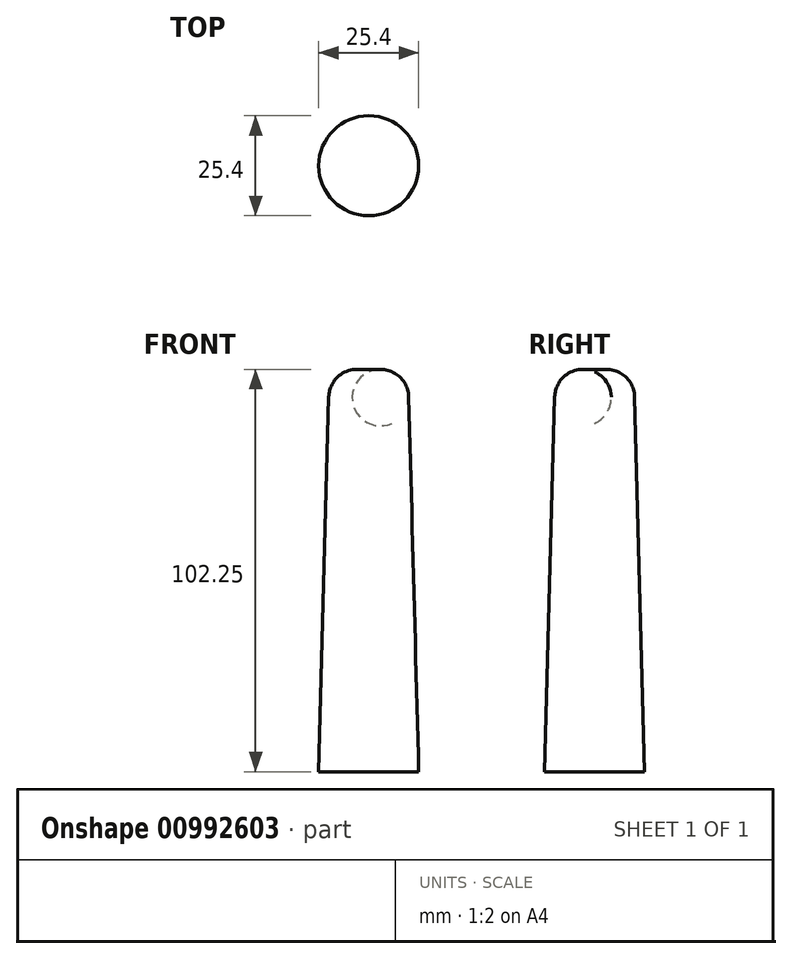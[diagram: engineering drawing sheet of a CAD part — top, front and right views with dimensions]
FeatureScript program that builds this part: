
annotation { "Feature Type Name" : "Feature", "Feature Type Description" : "" }
export const myFeature = defineFeature(function(context is Context, id is Id, definition is map)
    precondition{}
    {
        {
            var Q0;
            Q0=qCreatedBy(makeId("Front.planeOp"),FACE);
            var sketch = newSketch(context, id + "F0", { "sketchPlane" : qUnion([Q0])});
            skLineSegment(sketch, "E0", {"start": v(0, 101.6) * mm, "end": v(0, 0) * mm});
            skLineSegment(sketch, "E1", {"start": v(0, 0) * mm, "end": v(-12.7, 0) * mm});
            skLineSegment(sketch, "E2", {"start": v(-12.7, 0) * mm, "end": v(-10.16, 95.25) * mm});
            skArc(sketch, "E3", {"start": v(0, 101.6) * mm, "mid": v(-6.78, 101.15) * mm, "end": v(-10.16, 95.25) * mm});
            skSolve(sketch);
        }
        {
            var Q0;
            Q0=makeQuery(id+"F0.imprint","IMPRINT",FACE,{"disambiguationData":[TD([[makeQuery(id+"F0.imprint","IMPRINT",EDGE,{"derivedFrom":sQuery(id+"F0.wireOp",EDGE,"E0")}),-1.0]])]});
            var Q1;
            Q1=sQuery(id+"F0.wireOp",EDGE,"E0");
            revolve(context, id + "F1", {"surfaceOperationType" : NewSurfaceOperationType.NEW, "entities" : qUnion([Q0]), "axis" : qUnion([Q1]), "revolveType" : RevolveType.FULL});
        }
    });
